# Revit family: TCAT14-SM
name_source: partatom
category: Lighting Fixtures
revit_build: Autodesk Revit Architecture 2012 (Build: 20110309_2315(x64)
units: mm (PartAtom-declared; Revit-internal decimal feet)

## types (1)
- TCAT14
    Apparent Load = 0 VA
    Backbox = Hubbell - White
    Certifications = UL1598, 2108 & CSA
    Default Elevation = 48 "
    Description = 1'x 4'LED Twin Contempory Architectural Troffer.
    Height = 4.625 "
    Lamp = LED Lamp
    Light Bulb = Hubbell - White Glass
    Load Classification = Lighting
    Manufacturer = Columbia Lighting
    Manufacturer Fax = (866)-898-1065
    Model = TCAT14-SM
    Photometric Web = Web TCAT14 : TCAT14-30MWx-EDU
    Row Length = 48 "
    URL = http://www.columbialighting.com
    Voltage = 120 V
    Warranty = Five-year warranty.
    Wattage Comments = 21-58 W
    Watts = 58 W
    Width = 12 "
    zz Length = 47 "

## geometry (parser evidence)
native form markers: Sweep x8
no freeform markers — native parametric forms only
